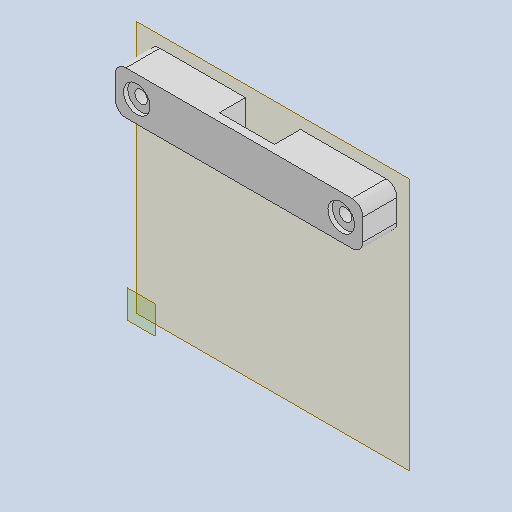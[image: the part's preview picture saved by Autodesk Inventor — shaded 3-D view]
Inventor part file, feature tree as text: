
AUTODESK INVENTOR PART (.ipt)
format: ipt  version: 2023 (Build 270158000, 158)  size: 130,560 bytes
history: native  units: mm
features: reference x6, other x4, extrude x3, sketch x3, plane x2, projected_geometry x1
ambient origin geometry x8: Origin, YZ Plane, XZ Plane, XY Plane, X Axis, Y Axis, Z Axis, Center Point
bodies: Solid1 (feature_tree)
feature tree (19):
  plane  "Work Plane1"
  extrude  "Extrusion1"  Depth=7.842mm
  extrude  "Extrusion2"  Depth=0.175mm
  plane  "Work Plane2"
  extrude  "Extrusion3"  Depth=12.908mm TaperAngle=0.0deg
  sketch  "Sketch1"  dims[d0=7.842mm d1=0.0mm d2=0.1mm]
  reference  "Reference1"
  reference  "Reference2"
  reference  "Reference3"
  sketch  "Sketch2"  dims[d3=0.1mm d4=0.175mm]
  sketch  "Sketch3"  dims[d5=12.908mm d6=0.0mm d7=12.908mm d8=0.0mm]
  projected_geometry  "Projected Loop1"
  reference  "Reference4"
  reference  "Reference5"
  reference  "Reference6"
  parser-record x1  (decoder bookkeeping rows leaked as tree rows — omitted from the tree; the rows remain in map.json)
  other  "Assembly_V6.iam"
  other  "house_V6:1"
  other  "longerScrew:1"
note: 1 file-system path scrubbed to <path> (originals preserved in map.json)
